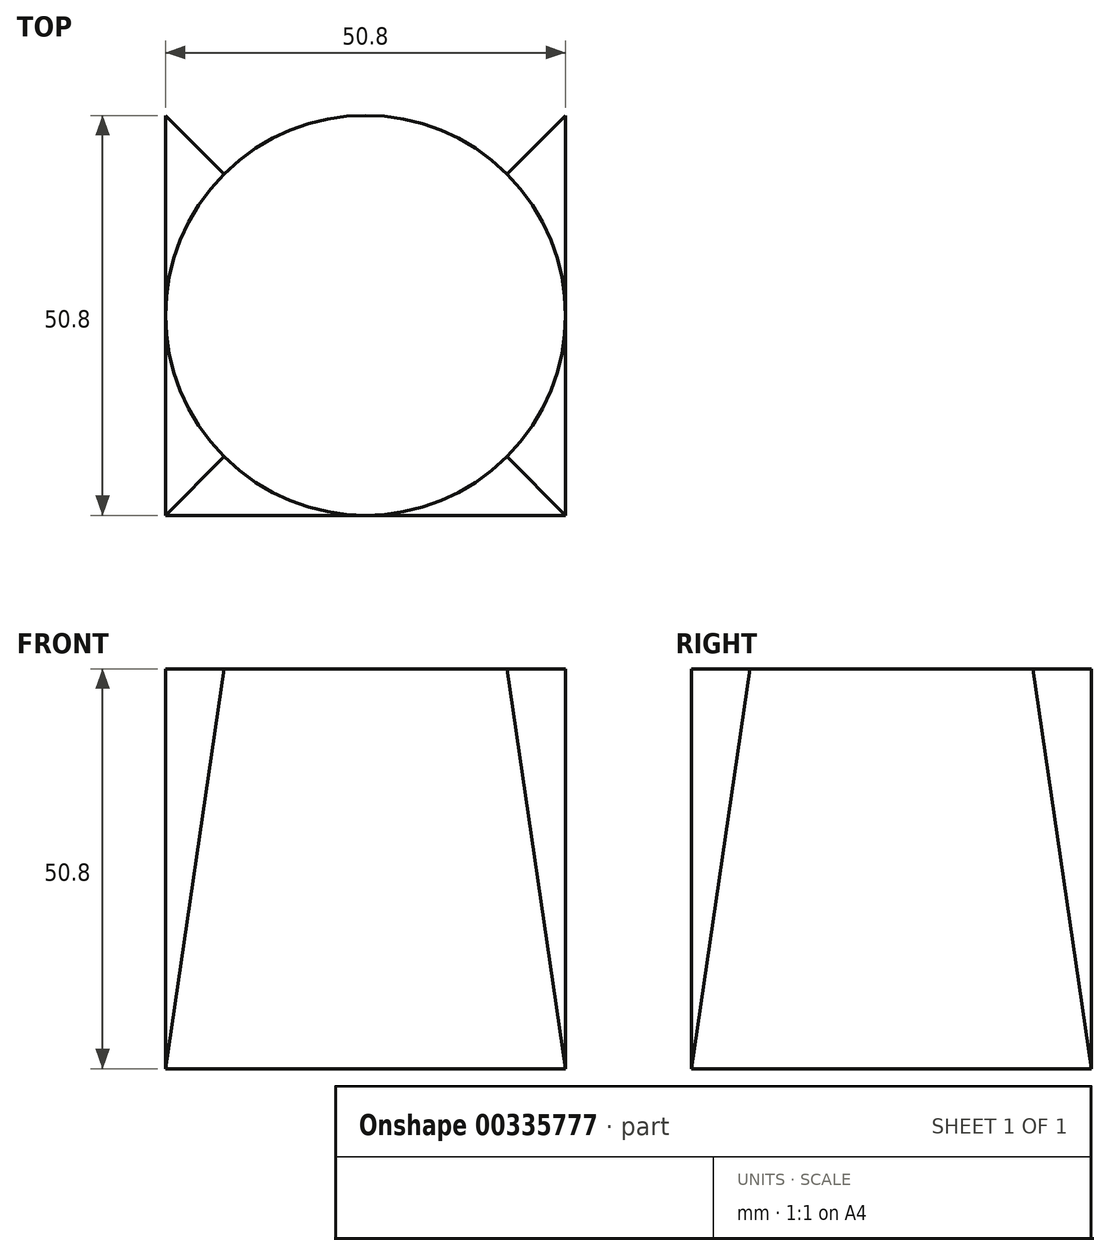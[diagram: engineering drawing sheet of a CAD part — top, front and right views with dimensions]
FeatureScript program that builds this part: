
annotation { "Feature Type Name" : "Feature", "Feature Type Description" : "" }
export const myFeature = defineFeature(function(context is Context, id is Id, definition is map)
    precondition{}
    {
        {
            var Q0;
            Q0=qCreatedBy(makeId("Top.planeOp"),FACE);
            var sketch = newSketch(context, id + "F0", { "sketchPlane" : qUnion([Q0])});
            skLineSegment(sketch, "E0.bottom", {"start": v(-25.4, 25.4) * mm, "end": v(25.4, 25.4) * mm});
            skLineSegment(sketch, "E0.top", {"start": v(-25.4, -25.4) * mm, "end": v(25.4, -25.4) * mm});
            skLineSegment(sketch, "E0.left", {"start": v(-25.4, 25.4) * mm, "end": v(-25.4, -25.4) * mm});
            skLineSegment(sketch, "E0.right", {"start": v(25.4, 25.4) * mm, "end": v(25.4, -25.4) * mm});
            skSolve(sketch);
        }
        {
            var Q0;
            Q0=qCreatedBy(makeId("Top.planeOp"),FACE);
            cPlane(context, id + "F1", {"entities" : qUnion([Q0]), "cplaneType" : CPlaneType.OFFSET, "offset" : 50.8 * mm, "width" : 152.4 * mm, "height" : 152.4 * mm});
        }
        {
            var Q0;
            Q0=qCreatedBy(id+"F1.planeOp",FACE);
            var sketch = newSketch(context, id + "F2", { "sketchPlane" : qUnion([Q0])});
            skCircle(sketch, "E1", {"center": v(0, 0) * mm, "radius": 25.4 * mm});
            skSolve(sketch);
        }
        {
            var Q0;
            Q0=makeQuery(id+"F0.imprint","IMPRINT",FACE,{"disambiguationData":[TD([[makeQuery(id+"F0.imprint","IMPRINT",EDGE,{"derivedFrom":sQuery(id+"F0.wireOp",EDGE,"E0.bottom")}),-1.0]])]});
            var Q1;
            Q1=makeQuery(id+"F2.imprint","IMPRINT",FACE,{"disambiguationData":[TD([[makeQuery(id+"F2.imprint","IMPRINT",EDGE,{"derivedFrom":sQuery(id+"F2.wireOp",EDGE,"E1")}),1.0]])]});
            loft(context, id + "F3", {"sheetProfilesArray" : [{ "sheetProfileEntities" : qUnion([Q0]) }, { "sheetProfileEntities" : qUnion([Q1]) }]});
        }
    });
